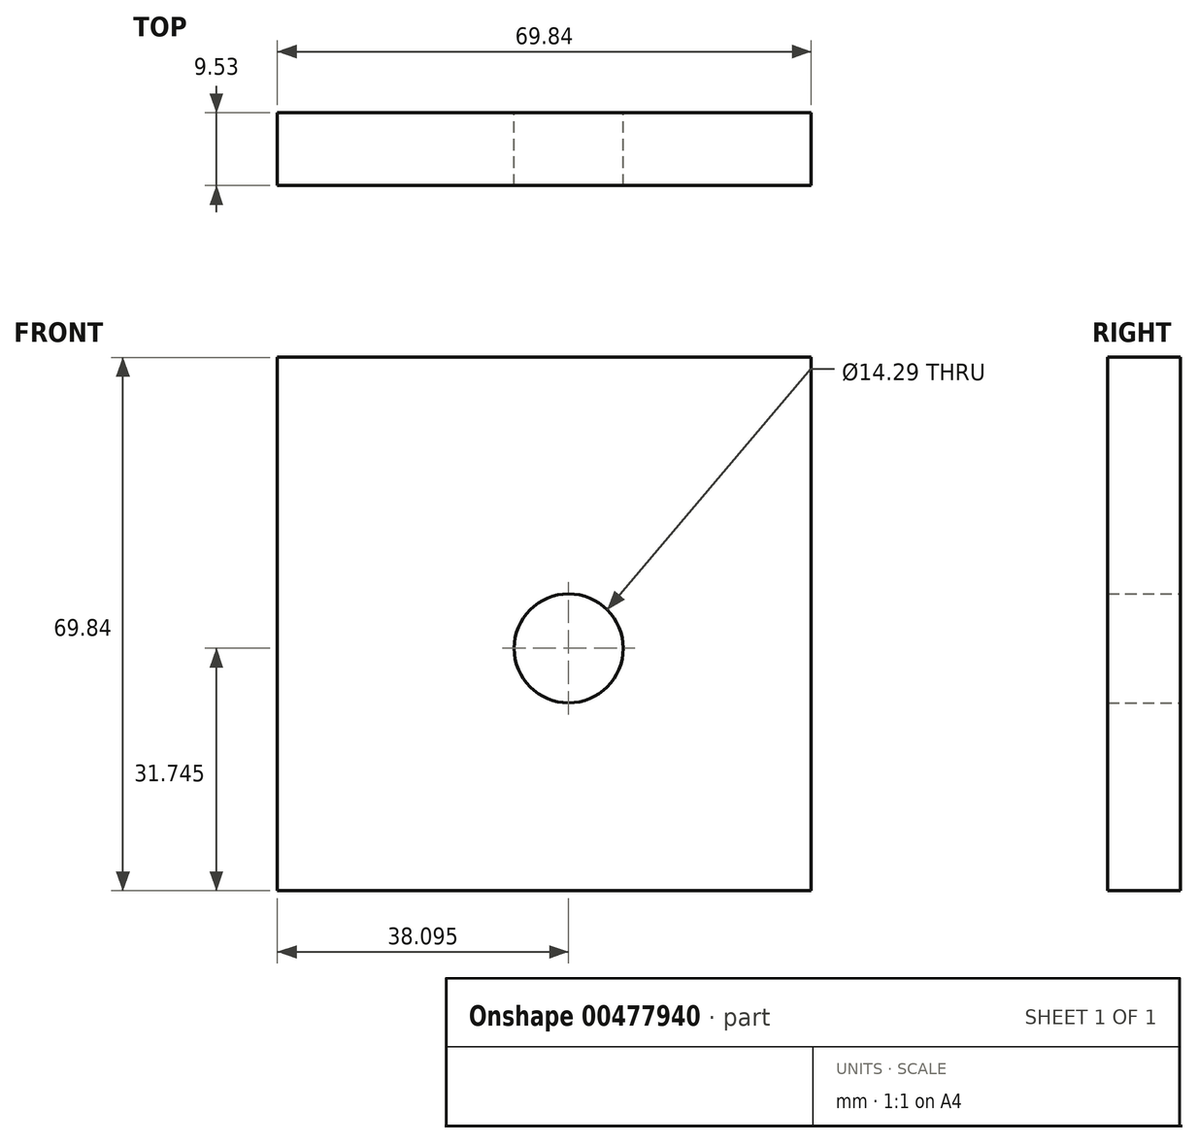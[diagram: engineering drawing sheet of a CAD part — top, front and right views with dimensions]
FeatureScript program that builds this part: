
annotation { "Feature Type Name" : "Feature", "Feature Type Description" : "" }
export const myFeature = defineFeature(function(context is Context, id is Id, definition is map)
    precondition{}
    {
        {
            var Q0;
            Q0=qCreatedBy(makeId("Front.planeOp"),FACE);
            var sketch = newSketch(context, id + "F0", { "sketchPlane" : qUnion([Q0])});
            skLineSegment(sketch, "E0.bottom", {"start": v(34.93, -34.92) * mm, "end": v(-34.93, -34.92) * mm});
            skLineSegment(sketch, "E0.top", {"start": v(34.93, 34.93) * mm, "end": v(-34.93, 34.92) * mm});
            skLineSegment(sketch, "E0.left", {"start": v(34.93, -34.92) * mm, "end": v(34.93, 34.93) * mm});
            skLineSegment(sketch, "E0.right", {"start": v(-34.93, -34.93) * mm, "end": v(-34.93, 34.92) * mm});
            skCircle(sketch, "E1", {"center": v(3.18, -3.18) * mm, "radius": 7.14 * mm});
            skSolve(sketch);
        }
        {
            var Q0;
            Q0 = qSketchRegion(id + "F0", true);
            extrude(context, id + "F1", {"entities" : qUnion([Q0]), "depth" : 9.52 * mm});
        }
    });
